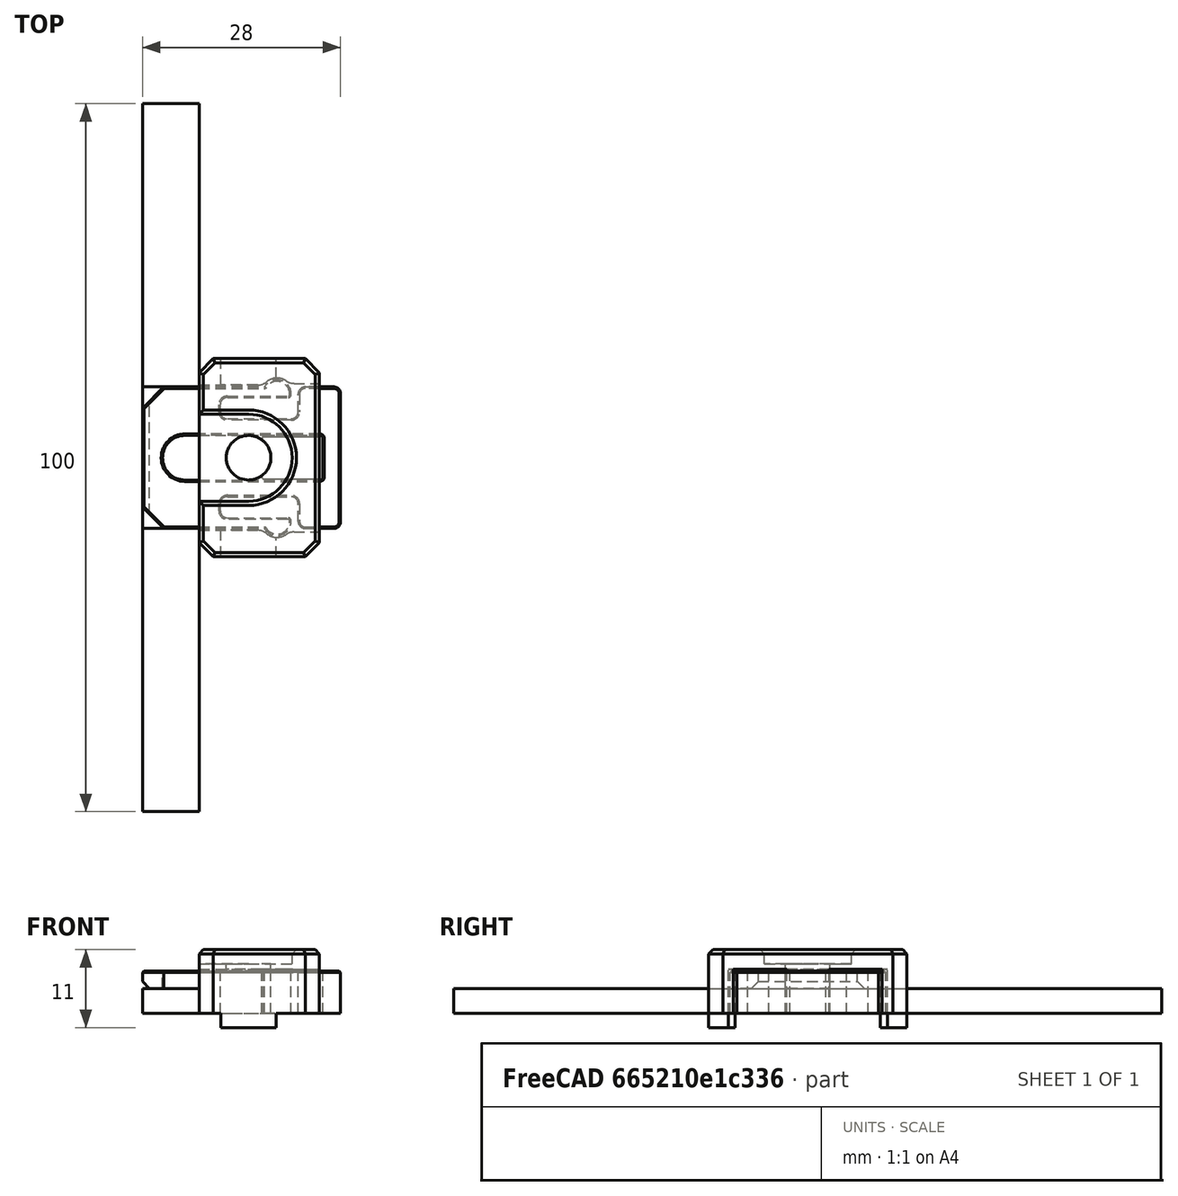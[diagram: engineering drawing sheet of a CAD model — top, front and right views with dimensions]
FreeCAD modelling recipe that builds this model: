
FCSTD DOCUMENT  (FreeCAD 0.19R24291 (Git))
Label: panel-mount-quick-release
License: Other
LicenseURL: GPL3
objects: Part::Box×18, Part::MultiFuse×11, Part::Cylinder×10, Part::Cut×8, Part::Fillet×7, Part::Chamfer×6, Part::Refine×3, Part::Feature×2
note: 65 computed .brp shape members not serialized (recipe doc carries the construction recipe); baked Part::Feature solids carry a one-line shape summary decoded from their .brp

FEATURE [Part::Box] Box  label="Cube"
  AttacherType = Attacher::AttachEngine3D
  Height = 3.5
  Length = 8
  Placement = pos=(0,-50,0) rot=(0,0,1;0rad)
  Width = 100
FEATURE [Part::Box] Box001  label="Cube001"
  AttacherType = Attacher::AttachEngine3D
  Height = 6
  Length = 21
  Placement = pos=(0,-10,0) rot=(0,0,1;0rad)
  Width = 20
FEATURE [Part::Box] Box002  label="Cube002"
  AttacherType = Attacher::AttachEngine3D
  Height = 3.5
  Length = 8
  Placement = pos=(0,-10,0) rot=(0,0,1;0rad)
  Width = 20
FEATURE [Part::Box] Box003  label="Cube003"
  AttacherType = Attacher::AttachEngine3D
  Height = 3.5
  Length = 8
  Placement = pos=(0,-10,0) rot=(0,0,1;0rad)
  Width = 20
FEATURE [Part::Cut] Cut
  Base = -> Box001
  Tool = -> Box003
FEATURE [Part::Chamfer] Chamfer
  Base = -> Cut
  Edges = 2 edges r=3: [Edge1,Edge3]
FEATURE [Part::Cylinder] Cylinder
  Angle = 360
  AttacherType = Attacher::AttachEngine3D
  Height = 10
  Placement = pos=(6,0,0) rot=(0,0,1;0rad)
  Radius = 3.15
FEATURE [Part::Box] Box004  label="Cube004"
  AttacherType = Attacher::AttachEngine3D
  Height = 10
  Length = 15
  Placement = pos=(6,-3.15,0) rot=(0,0,1;0rad)
  Width = 6.3
FEATURE [Part::Chamfer] Chamfer001
  Base = -> Chamfer
  Edges = 1 edges r=1: [Edge3]
FEATURE [Part::Cylinder] Cylinder001
  Angle = 360
  AttacherType = Attacher::AttachEngine3D
  Height = 6
  Placement = pos=(19,9,0) rot=(0,0,1;0rad)
  Radius = 2
FEATURE [Part::Cylinder] Cylinder002
  Angle = 360
  AttacherType = Attacher::AttachEngine3D
  Height = 6
  Placement = pos=(19,-9,0) rot=(0,0,1;0rad)
  Radius = 2
FEATURE [Part::Box] Box005  label="Cube005"
  AttacherType = Attacher::AttachEngine3D
  Height = 10
  Length = 10
  Placement = pos=(11,-8,0) rot=(0,0,1;0rad)
  Width = 3
FEATURE [Part::Fillet] Fillet
  Base = -> Box005
  Edges = 2 edges r=1: [Edge1,Edge3]
  Placement = pos=(0,-0.5,0) rot=(0,0,1;0rad)
FEATURE [Part::Feature] Fillet001
  Placement = pos=(0,13.5,0) rot=(0,0,1;0rad)
  shape: bbox 10 x 3 x 10 mm, 8 faces (baked)
FEATURE [Part::Cylinder] Cylinder004
  Angle = 360
  AttacherType = Attacher::AttachEngine3D
  Height = 6.25
  Placement = pos=(19,9,0) rot=(0,0,1;0rad)
  Radius = 2.25
FEATURE [Part::Cylinder] Cylinder005
  Angle = 360
  AttacherType = Attacher::AttachEngine3D
  Height = 6.25
  Placement = pos=(19,-9,0) rot=(0,0,1;0rad)
  Radius = 2.25
FEATURE [Part::MultiFuse] Fusion004
  Shapes = -> [Fillet,Fillet001]
FEATURE [Part::Cylinder] Cylinder006
  Angle = 360
  AttacherType = Attacher::AttachEngine3D
  Height = 6.25
  Placement = pos=(28,9,0) rot=(0,0,1;0rad)
  Radius = 2.25
FEATURE [Part::Cylinder] Cylinder007
  Angle = 360
  AttacherType = Attacher::AttachEngine3D
  Height = 6.25
  Placement = pos=(28,-9,0) rot=(0,0,1;0rad)
  Radius = 2.25
FEATURE [Part::Box] Box006  label="Cube006"
  AttacherType = Attacher::AttachEngine3D
  Height = 6.25
  Length = 10
  Placement = pos=(8,-10.25,0) rot=(0,0,1;0rad)
  Width = 20.5
FEATURE [Part::Box] Box007  label="Cube007"
  AttacherType = Attacher::AttachEngine3D
  Height = 6.25
  Length = 12
  Placement = pos=(18,-10.5,0) rot=(0,0,1;0rad)
  Width = 21
FEATURE [Part::MultiFuse] Fusion005  label="inner-cut"
  Shapes = -> [Box006,Box007,Cylinder005,Cylinder007,Cylinder004,Cylinder006]
FEATURE [Part::Box] Box008  label="Cube008"
  AttacherType = Attacher::AttachEngine3D
  Height = 9
  Length = 17
  Placement = pos=(8,-14,0) rot=(0,0,1;0rad)
  Width = 28
FEATURE [Part::MultiFuse] Fusion
  Shapes = -> [Box004,Cylinder]
FEATURE [Part::Cut] Cut005
  Base = -> Chamfer001
  Tool = -> Fusion
FEATURE [Part::Fillet] Fillet002
  Base = -> Cut005
  Edges = 2 edges r=1: [Edge28,Edge31]
FEATURE [Part::MultiFuse] Fusion008
  Shapes = -> [Cylinder002,Cylinder001]
FEATURE [Part::MultiFuse] Fusion009
  Shapes = -> [Fillet002,Fusion008]
FEATURE [Part::Cut] Cut006
  Base = -> Fusion009
  Tool = -> Fusion004
FEATURE [Part::Refine] Cut006001
  Source = -> Cut006
FEATURE [Part::Fillet] Fillet003
  Base = -> Cut006001
  Edges = 6 edges r=0.4: [Edge30,Edge43,Edge47,Edge55,Edge60,Edge74]
FEATURE [Part::Cylinder] Cylinder013
  Angle = 360
  AttacherType = Attacher::AttachEngine3D
  Height = 10
  Placement = pos=(15,0,8) rot=(0,0,1;0rad)
  Radius = 6.15
FEATURE [Part::Cut] Cut006002
  Base = -> Box008
  Tool = -> Fusion005
FEATURE [Part::Cylinder] Cylinder014
  Angle = 360
  AttacherType = Attacher::AttachEngine3D
  Height = 10
  Placement = pos=(15,0,0) rot=(0,0,1;0rad)
  Radius = 3.15
FEATURE [Part::Cylinder] Cylinder015
  Angle = 360
  AttacherType = Attacher::AttachEngine3D
  Height = 10
  Placement = pos=(15,0,0) rot=(0,0,1;0rad)
  Radius = 3.15
FEATURE [Part::Cut] Cut006003
  Base = -> Cut006002
  Tool = -> Cylinder015
FEATURE [Part::Box] Box009  label="Cube009"
  AttacherType = Attacher::AttachEngine3D
  Height = 7
  Length = 10
  Placement = pos=(15,-3,0) rot=(0,0,1;0rad)
  Width = 6
FEATURE [Part::Cut] Cut006004
  Base = -> Box009
  Tool = -> Cylinder014
FEATURE [Part::Chamfer] Chamfer005
  Base = -> Cut006004
  Edges = 2 edges r=1: [Edge4,Edge15]
FEATURE [Part::MultiFuse] Fusion010
  Shapes = -> [Chamfer005,Cut006003]
FEATURE [Part::Chamfer] Chamfer006
  Base = -> Fusion010
  Edges = 4 edges r=2: [Edge44,Edge50,Edge73,Edge76]
FEATURE [Part::Box] Box010  label="Cube010"
  AttacherType = Attacher::AttachEngine3D
  Height = 2
  Length = 7.8
  Placement = pos=(11.1,-14,-2) rot=(0,0,1;0rad)
  Width = 4
FEATURE [Part::Box] Box011  label="Cube011"
  AttacherType = Attacher::AttachEngine3D
  Height = 2
  Length = 7.8
  Placement = pos=(11.1,10,-2) rot=(0,0,1;0rad)
  Width = 4
FEATURE [Part::MultiFuse] Fusion011
  Shapes = -> [Box011,Box010]
FEATURE [Part::Feature] Fusion005001  label="inner-cut001"
  Placement = pos=(0,0,-2) rot=(0,0,1;0rad)
  shape: bbox 22.25 x 22.5 x 6.25 mm, 50 faces (baked)
FEATURE [Part::Cut] Cut006006
  Base = -> Fusion011
  Tool = -> Fusion005001
FEATURE [Part::Box] Box012  label="Cube012"
  AttacherType = Attacher::AttachEngine3D
  Height = 10
  Length = 10
  Placement = pos=(5,-6.15,8) rot=(0,0,1;0rad)
  Width = 12.3
FEATURE [Part::MultiFuse] Fusion005002
  Placement = pos=(0,0,-1) rot=(0,0,1;0rad)
  Shapes = -> [Box012,Cylinder013]
FEATURE [Part::Box] Box013  label="Cube013"
  AttacherType = Attacher::AttachEngine3D
  Height = 6
  Length = 6
  Placement = pos=(20,-5.5,0) rot=(0,0,1;0rad)
  Width = 2.35
FEATURE [Part::Box] Box014  label="Cube014"
  AttacherType = Attacher::AttachEngine3D
  Height = 6
  Length = 6
  Placement = pos=(20,3.15,0) rot=(0,0,1;0rad)
  Width = 2.35
FEATURE [Part::Box] Box015  label="Cube015"
  AttacherType = Attacher::AttachEngine3D
  Height = 6
  Length = 2.5
  Placement = pos=(25.5,-6.5,0) rot=(0,0,1;0rad)
  Width = 13
FEATURE [Part::Box] Box016  label="Cube016"
  AttacherType = Attacher::AttachEngine3D
  Height = 6
  Length = 6
  Placement = pos=(22,-10,0) rot=(0,0,1;0rad)
  Width = 5
FEATURE [Part::Box] Box017  label="Cube017"
  AttacherType = Attacher::AttachEngine3D
  Height = 6
  Length = 6
  Placement = pos=(22,5,0) rot=(0,0,1;0rad)
  Width = 5
FEATURE [Part::MultiFuse] Fusion005003
  Shapes = -> [Box017,Box016,Box015,Box014,Box013]
FEATURE [Part::Fillet] Fillet004
  Base = -> Fusion005003
  Edges = 4 edges r=1: [Edge26,Edge29,Edge94,Edge97]
FEATURE [Part::MultiFuse] Fusion005004
  Shapes = -> [Fillet003,Fillet004]
FEATURE [Part::Refine] Fusion005004001
  Source = -> Fusion005004
FEATURE [Part::Fillet] Fillet005
  Base = -> Fusion005004001
  Edges = 2 edges r=1: [Edge93,Edge103]
FEATURE [Part::Fillet] Fillet006
  Base = -> Fillet005
  Edges = 2 edges r=0.4: [Edge78,Edge85]
FEATURE [Part::Chamfer] Chamfer008
  Base = -> Fillet006
  Edges = 38 edges r=0.2: [Edge40,Edge42,Edge46,Edge51,Edge52,Edge55,Edge56,Edge60,Edge64,Edge69,Edge71,Edge72,Edge75,Edge76,Edge78,Edge80,Edge82,Edge85,Edge87,Edge89,Edge90,Edge92,Edge94,Edge96,Edge99,Edge100,Edge102,Edge104,Edge106,Edge108,Edge110,Edge113,Edge114,Edge116,Edge117,Edge118,Edge119,Edge120]
FEATURE [Part::Refine] Chamfer008001
  Source = -> Chamfer008
FEATURE [Part::Cut] Cut006007
  Base = -> Chamfer006
  Tool = -> Fusion005002
FEATURE [Part::MultiFuse] Fusion005004002
  Shapes = -> [Cut006006,Cut006007]
FEATURE [Part::Fillet] Fillet007
  Base = -> Fusion005004002
  Edges = 4 edges r=2: [Edge23,Edge53,Edge71,Edge126]
FEATURE [Part::Chamfer] Chamfer008002
  Base = -> Fillet007
  Edges = 13 edges r=0.6: [Edge35,Edge49,Edge58,Edge71,Edge75,Edge80,Edge81,Edge82,Edge83,Edge84,Edge85,Edge86,Edge87]
